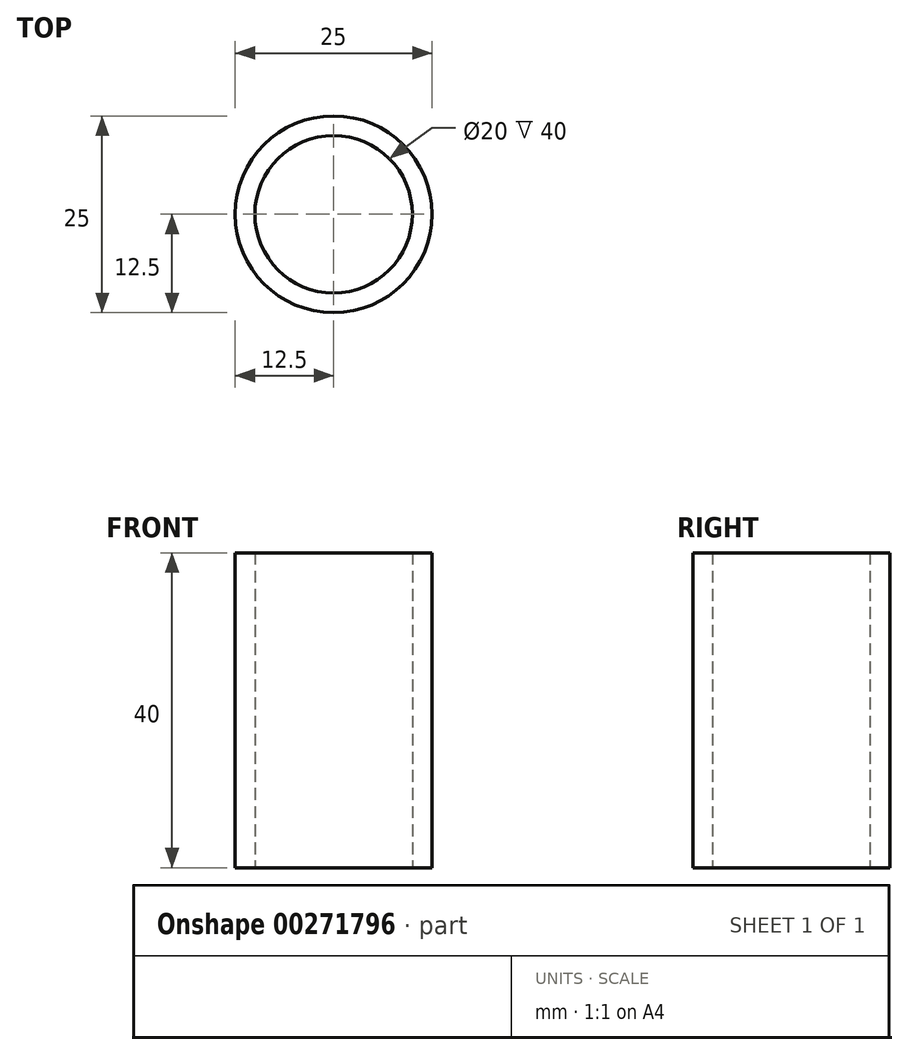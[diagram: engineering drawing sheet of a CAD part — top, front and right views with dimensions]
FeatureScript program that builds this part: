
annotation { "Feature Type Name" : "Feature", "Feature Type Description" : "" }
export const myFeature = defineFeature(function(context is Context, id is Id, definition is map)
    precondition{}
    {
        {
            var Q0;
            Q0=qCreatedBy(makeId("Top.planeOp"),FACE);
            var sketch = newSketch(context, id + "F0", { "sketchPlane" : qUnion([Q0])});
            skCircle(sketch, "E0", {"center": v(0, 0) * mm, "radius": 10 * mm});
            skCircle(sketch, "E1", {"center": v(0, 0) * mm, "radius": 12.5 * mm});
            skSolve(sketch);
        }
        {
            var Q0;
            Q0=makeQuery(id+"F0.imprint","IMPRINT",FACE,{"disambiguationData":[TD([[makeQuery(id+"F0.imprint","IMPRINT",EDGE,{"derivedFrom":sQuery(id+"F0.wireOp",EDGE,"E0")}),-1.0]])]});
            extrude(context, id + "F1", {"entities" : qUnion([Q0]), "depth" : 40 * mm});
        }
    });
